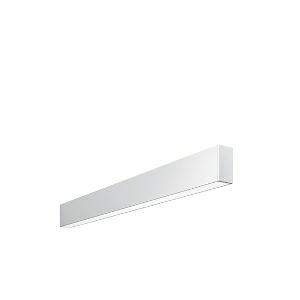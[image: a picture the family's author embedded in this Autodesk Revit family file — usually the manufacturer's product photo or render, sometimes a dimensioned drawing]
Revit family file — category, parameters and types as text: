
# Revit family: idoo_line_-_ilw_3000_840_d_00808324_55c6
name_source: partatom
category: Lighting Fixtures
units: mm (PartAtom-declared; Revit-internal decimal feet)

## family parameters
Cut with Voids When Loaded = No
Host = Face
Light Source = No
Part Type = Normal
Room Calculation Point = No
Round Connector Dimension = Use Diameter
Shared = No

## types (1)
- IDOO.line - ILW 3000/840/D (1 x LED, 3150 lm, 4000K)
    Apparent Load = 23 VA
    Approval mark = CE
    CIE Flux Codes = 66 91 98 40 100
    Color Rendering = 80-89
    Color Temperature = 4000K
    Control Gear = Electronic ballast
    Default Elevation = 2000 mm  [stored 6.56168 ft]
    Description = ILW 3000/840/D|Wall-mounted luminaire|light source:  |work equipment: Adjustable electronic ballast, digital DALI|connected load: 220-240V, 50/60Hz|Power consumption: approx. 23 W|standby: approx. 0,25|power factor: approx. 0,970|luminous flux: 3150 lm|luminous efficacy: 136 lm/W|light distribution: Direct/indirect|direct ratio: approx. 40 %|colour temperature: Cold white, ca. 4000 K|color rendering index (CRI): >= 80|chromaticity tolerance:  3 SDCM|technology: Continuously dimmable|operation: External|luminaire body|material: Sectional aluminium|colour: White|lamp cover: Acrylic (PMMA), Clear|weight (net): approx. 4.7 kg|mains lead: Connector|design: Mounted version|Fastening: Mounting rail|glare control: Prism aperture|luminance(L65): <= 2700 cd/m|unified glare rating(4H 8H): <=  16|special features: DALI Load 1x, TouchDIM - dimming via standard switch, Flicker-free, Suitable as emergency lighting|
    Frequency = 50 Hz
    Height = 110 mm
    Lamp = 1 x LED
    Lamp Light Flux = 3150 lm
    Lamp count = 1
    Length = 1134 mm
    Luminous efficacy = 137 lm/W
    Manufacturer = Waldmann
    ModVariant = No
    Model = 00808324
    Mounting Place = Wall
    Mounting Type = Surface mounted
    Number of Poles = 1
    OnlyDefault = Yes
    Power Factor = 1
    Product Name = IDOO.line - ILW 3000/840/D
    Product group = Wall mounted Luminaire
    ProductGroupID = 20
    Protection Class = Protection class I
    Protection Degree = IP 40
    RLX_Detail_Level = 1
    RLX_Emergency_Light_Flux = 0 lm
    RLX_Emergency_Type = 0
    RLX_Emergency_Type_DB = No
    RlxData = <blob elided: 32629 chars, md5=6e9f8992>
    Socket = socket
    Standby Power = 0 W
    System Light Flux = 3150 lm
    System Power = 23 W
    Type Comments = Product without accessories
    Type Image = 113967000-00757948.jpg
    URL = http://relux.com
    VarID = ---
    Voltage = 230 V
    Voltage Range = 220-240 V
    Weight = 0.00 kg
    Width = 60 mm  [stored 0.19685 ft]

note: [stored X ft] marks values corroborated as IEEE doubles in the binary element streams (Revit-internal decimal feet)

## geometry (parser evidence)
native form markers: Blend x4, Sweep x12
no freeform markers — native parametric forms only
